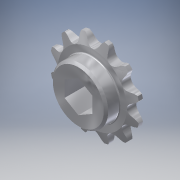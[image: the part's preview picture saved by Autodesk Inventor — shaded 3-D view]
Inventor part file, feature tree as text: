
AUTODESK INVENTOR PART (.ipt)
format: ipt  version: 2016 (Build 200138000, 138)  size: 485,376 bytes
history: native  units: in
note: dims shown in document units (in); Inventor stores cm internally (conversion verified against a paired STEP export)
features: chamfer x1
ambient origin geometry x8: Origin, YZ Plane, XZ Plane, XY Plane, X Axis, Y Axis, Z Axis, Center Point
bodies: Solid1 (feature_tree)
feature tree (1):
  chamfer  "Chamfer1"  [1 undecoded]
note: 1 required parameter value undecoded (feature->parameter linkage not recoverable at this tier; creation-order binding heuristic only, values carry confidence <= 0.55)
